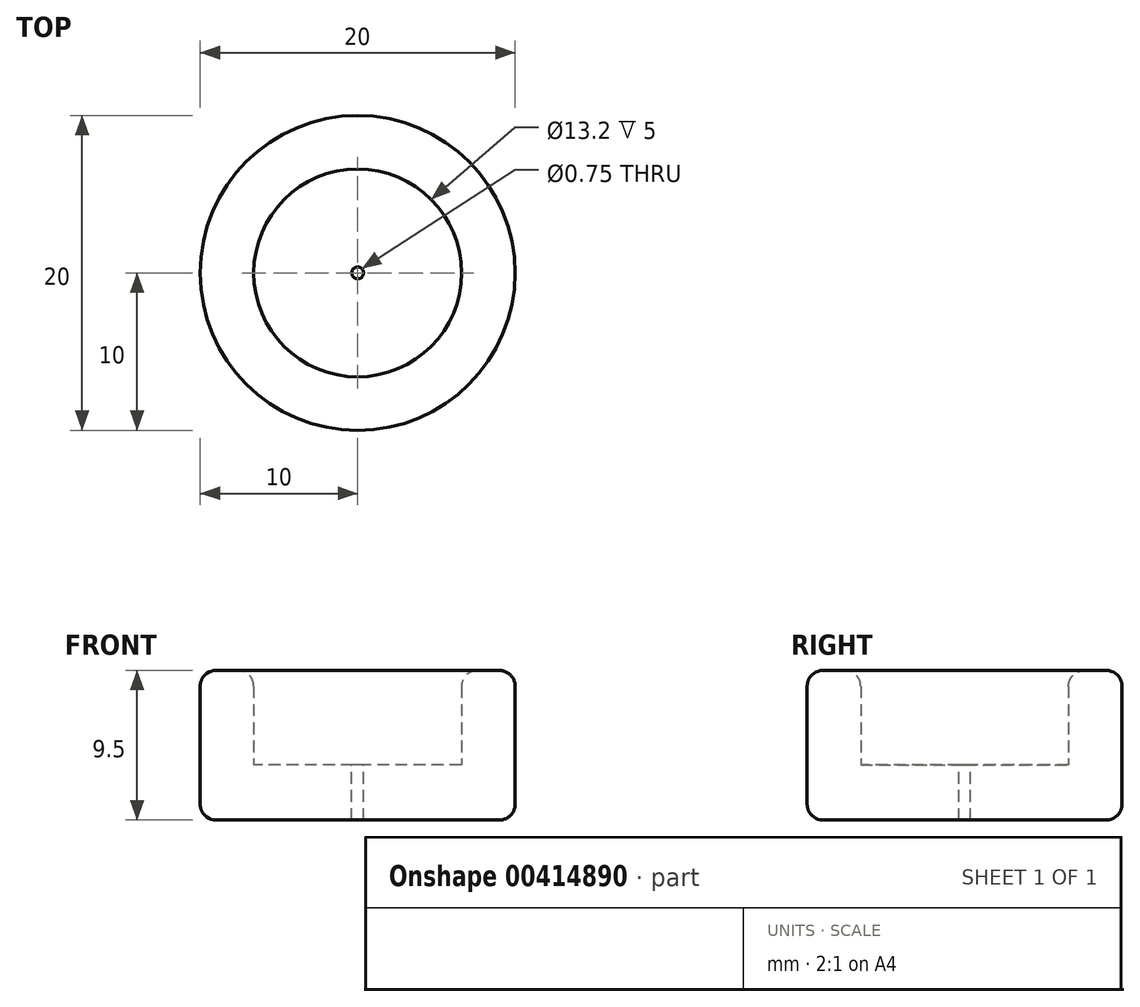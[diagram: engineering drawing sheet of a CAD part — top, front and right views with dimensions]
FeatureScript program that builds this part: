
annotation { "Feature Type Name" : "Feature", "Feature Type Description" : "" }
export const myFeature = defineFeature(function(context is Context, id is Id, definition is map)
    precondition{}
    {
        {
            var Q0;
            Q0=qCreatedBy(makeId("Top.planeOp"),FACE);
            var sketch = newSketch(context, id + "F0", { "sketchPlane" : qUnion([Q0])});
            skCircle(sketch, "E0", {"center": v(0, 0) * mm, "radius": 10 * mm});
            skSolve(sketch);
        }
        {
            var Q0;
            Q0 = qSketchRegion(id + "F0", true);
            var Q1;
            Q1=makeQuery(id+"F0.imprint","IMPRINT",FACE,{"disambiguationData":[TD([[makeQuery(id+"F0.imprint","IMPRINT",EDGE,{"derivedFrom":sQuery(id+"F0.wireOp",EDGE,"UlGXe3JW-qBB9-Whef-HEUH-JptGj8hReMEJ")}),1.0]])]});
            extrude(context, id + "F1", {"entities" : qUnion([Q0, Q1]), "oppositeDirection" : true, "depth" : 3.5 * mm});
        }
        {
            var Q0;
            Q0=makeQuery(id+"F1.opExtrude","CAP_FACE",FACE,{"disambiguationData":[OSD([sQuery(id+"F0.wireOp",EDGE,"E0")])],"isStart":true});
            var sketch = newSketch(context, id + "F2", { "sketchPlane" : qUnion([Q0])});
            skCircle(sketch, "E1", {"center": v(0, 0) * mm, "radius": 6.6 * mm});
            skSolve(sketch);
        }
        {
            var Q0;
            Q0=makeQuery(id+"F2.imprint","IMPRINT",FACE,{"disambiguationData":[TD([[makeQuery(id+"F2.imprint","IMPRINT",EDGE,{"derivedFrom":sQuery(id+"F2.wireOp",EDGE,"E1")}),-1.0]])]});
            extrude(context, id + "F3", {"entities" : qUnion([Q0]), "operationType" : NewBodyOperationType.ADD, "depth" : 6 * mm});
        }
        {
            var Q0;
            Q0=makeQuery(id+"F3.opExtrude","CAP_EDGE",EDGE,{"disambiguationData":[OSD([sQuery(id+"F2.wireOp",EDGE,"E1")])],"isStart":false});
            var Q1;
            Q1=makeQuery(id+"F1.opExtrude","CAP_EDGE",EDGE,{"disambiguationData":[OSD([sQuery(id+"F0.wireOp",EDGE,"E0")])],"isStart":false});
            fillet(context, id + "F4", {"entities" : qUnion([Q0, Q1]), "radius" : 1 * mm, "tangentPropagation" : true, "allowEdgeOverflow" : false});
        }
        {
            var Q0;
            Q0=makeQuery(id+"F3.opExtrude","CAP_EDGE",EDGE,{"disambiguationData":[OSD([sQuery(id+"F0.wireOp",EDGE,"E0")])],"isStart":false});
            fillet(context, id + "F5", {"entities" : qUnion([Q0]), "radius" : 1 * mm, "tangentPropagation" : true, "allowEdgeOverflow" : false});
        }
        {
            var Q0;
            Q0=makeQuery(id+"F1.opExtrude","CAP_FACE",FACE,{"disambiguationData":[OSD([sQuery(id+"F0.wireOp",EDGE,"E0")])],"isStart":true});
            var sketch = newSketch(context, id + "F6", { "sketchPlane" : qUnion([Q0])});
            skCircle(sketch, "E2", {"center": v(0, 0) * mm, "radius": 0.38 * mm});
            skSolve(sketch);
        }
        {
            var Q0;
            Q0=makeQuery(id+"F6.imprint","IMPRINT",FACE,{"disambiguationData":[TD([[makeQuery(id+"F6.imprint","IMPRINT",EDGE,{"derivedFrom":sQuery(id+"F6.wireOp",EDGE,"E2")}),1.0]])]});
            extrude(context, id + "F7", {"entities" : qUnion([Q0]), "operationType" : NewBodyOperationType.REMOVE, "endBound" : BoundingType.THROUGH_ALL, "oppositeDirection" : true, "depth" : .5 * mm});
        }
    });
